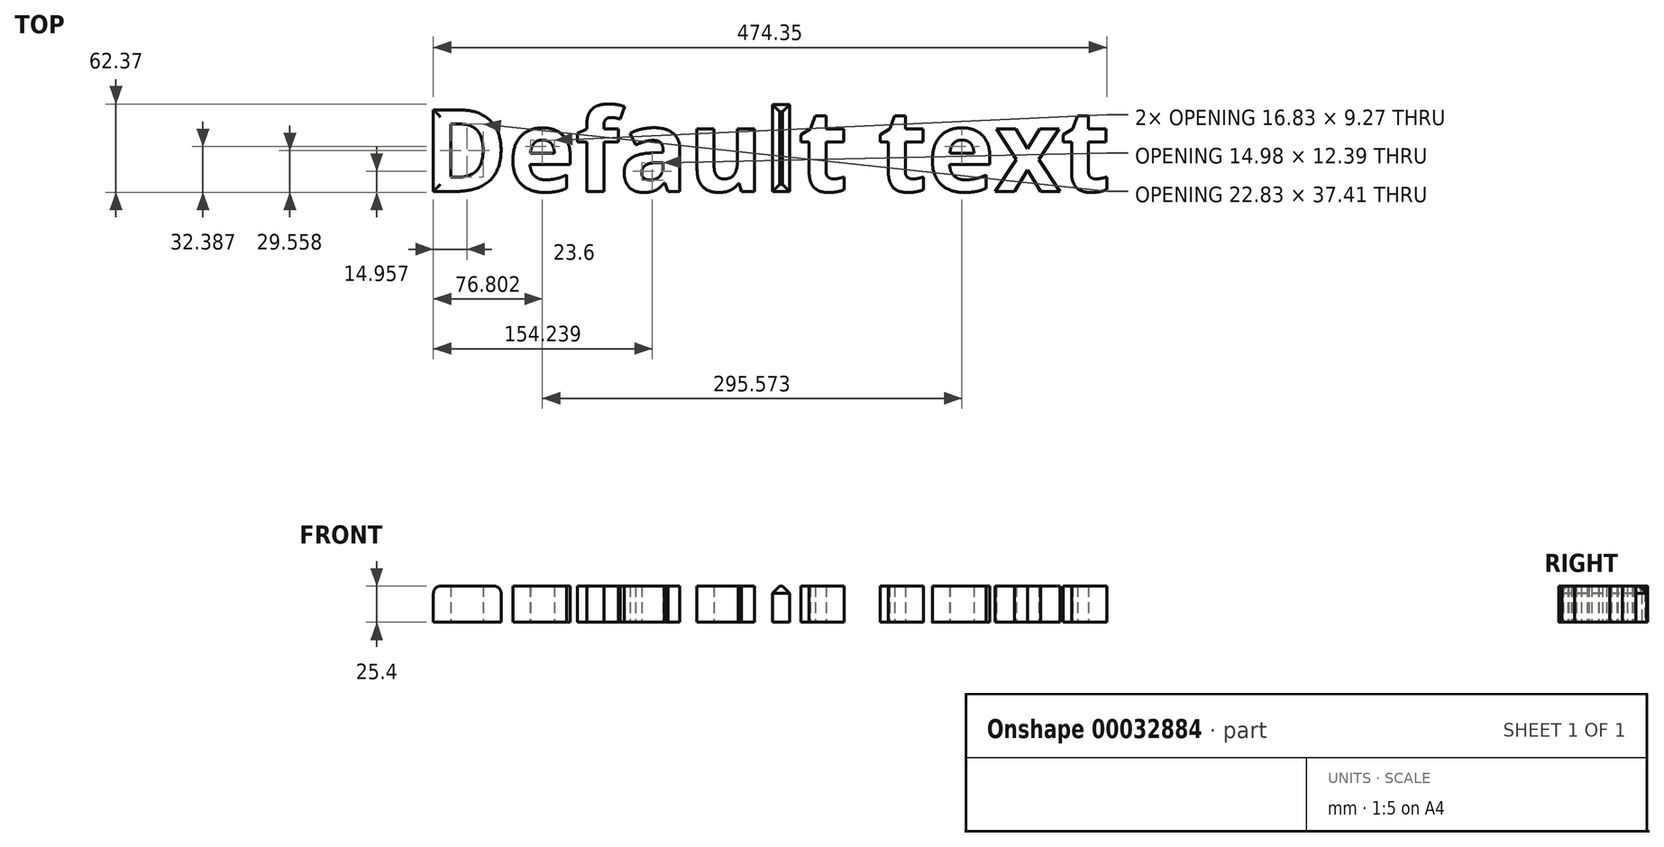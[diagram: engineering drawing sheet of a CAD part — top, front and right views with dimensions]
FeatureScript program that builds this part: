
annotation { "Feature Type Name" : "Feature", "Feature Type Description" : "" }
export const myFeature = defineFeature(function(context is Context, id is Id, definition is map)
    precondition{}
    {
        {
            var Q0;
            Q0=qCreatedBy(makeId("Top.planeOp"),FACE);
            var sketch = newSketch(context, id + "F0", { "sketchPlane" : qUnion([Q0])});
            skText(sketch, "E0", { "text": "Default text", "fontName": "OpenSans-Bold.ttf"});
            const initialGuessF0  = {"E0": [-0.1158, -0.02835, 1, 0, 0.05795]};
            skSetInitialGuess(sketch, initialGuessF0);
            skSolve(sketch);
        }
        {
            var Q0;
            Q0 = qSketchRegion(id + "F0", true);
            extrude(context, id + "F1", {"entities" : qUnion([Q0]), "depth" : 25.4 * mm});
        }
        {
            var Q0;
            Q0=makeQuery(id+"F1.opExtrude","CAP_EDGE",EDGE,{"disambiguationData":[OSD([sQuery(id+"F0.wireOp",EDGE,"E0.sketch_text.stroke-3")])],"isStart":false});
            var Q1;
            Q1=makeQuery(id+"F1.opExtrude","CAP_EDGE",EDGE,{"disambiguationData":[OSD([sQuery(id+"F0.wireOp",EDGE,"E0.sketch_text.stroke-2")])],"isStart":false});
            fillet(context, id + "F2", {"entities" : qUnion([Q0, Q1]), "radius" : 5.08 * mm, "tangentPropagation" : true, "allowEdgeOverflow" : false});
        }
        {
            var Q0;
            Q0=makeQuery(id+"F1.opExtrude","CAP_EDGE",EDGE,{"disambiguationData":[OSD([sQuery(id+"F0.wireOp",EDGE,"E0.sketch_text.stroke-95")])],"isStart":false});
            var Q1;
            Q1=makeQuery(id+"F1.opExtrude","CAP_EDGE",EDGE,{"disambiguationData":[OSD([sQuery(id+"F0.wireOp",EDGE,"E0.sketch_text.stroke-94")])],"isStart":false});
            var Q2;
            Q2=makeQuery(id+"F1.opExtrude","CAP_EDGE",EDGE,{"disambiguationData":[OSD([sQuery(id+"F0.wireOp",EDGE,"E0.sketch_text.stroke-93")])],"isStart":false});
            var Q3;
            Q3=makeQuery(id+"F1.opExtrude","CAP_EDGE",EDGE,{"disambiguationData":[OSD([sQuery(id+"F0.wireOp",EDGE,"E0.sketch_text.stroke-92")])],"isStart":false});
            chamfer(context, id + "F3", {"entities" : qUnion([Q0, Q1, Q2, Q3]), "width" : 5.08 * mm, "tangentPropagation" : true});
        }
    });
